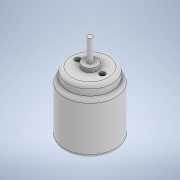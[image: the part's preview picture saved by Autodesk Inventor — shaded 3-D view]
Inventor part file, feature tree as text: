
AUTODESK INVENTOR PART (.ipt)
format: ipt  version: 2022 (Build 260153070, 153G)  size: 175,616 bytes
history: native  units: in
note: dims shown in document units (in); Inventor stores cm internally (conversion verified against a paired STEP export)
features: sketch x3, extrude x2, revolve x1, fillet x1, projected_geometry x1
ambient origin geometry x8: Origin, YZ Plane, XZ Plane, XY Plane, X Axis, Y Axis, Z Axis, Center Point
bodies: Body1 (feature_tree)
feature tree (8):
  revolve  "Revolution1"  [1 undecoded]
  fillet  "Fillet1"  Radius=0.0394in
  extrude  "Extrusion2"  TaperAngle=90.0deg  [1 undecoded]
  extrude  "Extrusion4"  Depth=0.1181in
  sketch  "Sketch3"  dims[d5=0.1673in d7=0.063in d10=0.0394in]
  sketch  "Sketch4"  dims[d13=0.0787in d14=90.0deg]
  sketch  "Sketch6"  dims[d15=0.0591in d16=0.1181in d17=0.315in d18=0.9843in d19=0.0591in d20=0.1575in d21=0.4134in d23=0.2461in d24=0.3937in d25=0.0906in d26=0.7874in d28=360.0deg d30=0.0787in d31=0.0in d34=0.0394in d35=0.0in]
  projected_geometry  "Projected Loop1"
note: 2 required parameter values undecoded (feature->parameter linkage not recoverable at this tier; creation-order binding heuristic only, values carry confidence <= 0.55)